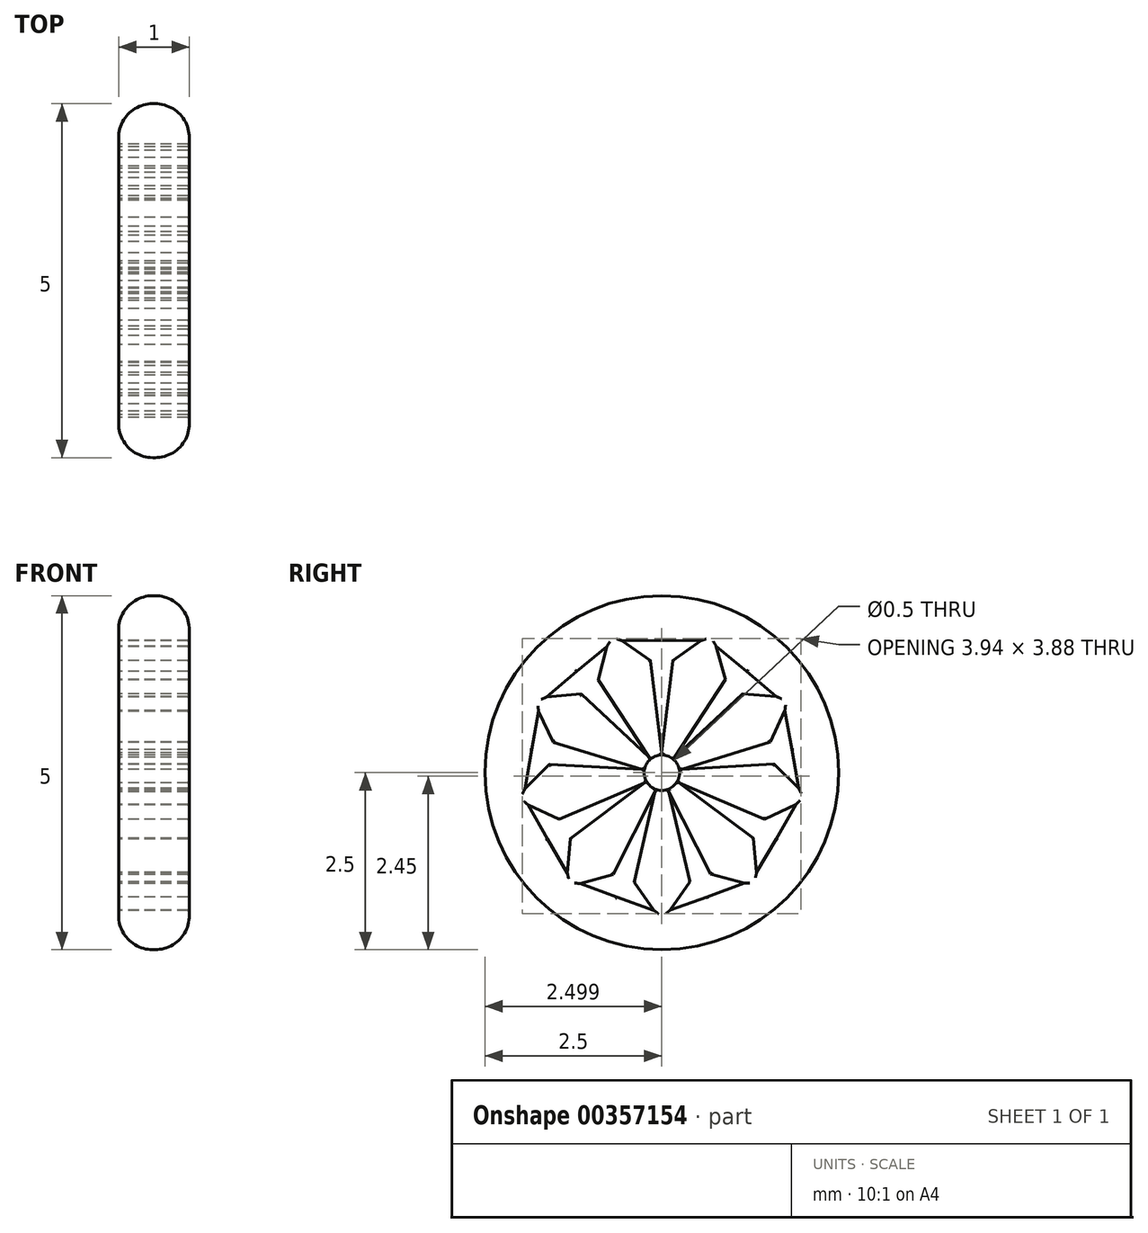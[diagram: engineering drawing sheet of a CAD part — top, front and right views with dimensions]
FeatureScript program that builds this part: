
annotation { "Feature Type Name" : "Feature", "Feature Type Description" : "" }
export const myFeature = defineFeature(function(context is Context, id is Id, definition is map)
    precondition{}
    {
        {
            var Q0;
            Q0=qCreatedBy(makeId("Right.planeOp"),FACE);
            var sketch = newSketch(context, id + "F0", { "sketchPlane" : qUnion([Q0])});
            skCircle(sketch, "E0", {"center": v(0, 0) * mm, "radius": 2.5 * mm});
            skCircle(sketch, "E1", {"center": v(0, 0) * mm, "radius": 2 * mm});
            skCircle(sketch, "E2", {"center": v(0, 0) * mm, "radius": 0.25 * mm});
            skLineSegment(sketch, "E3", {"start": v(0, 1.87) * mm, "end": v(-0.56, 1.86) * mm});
            skLineSegment(sketch, "E4", {"start": v(-0.16, 1.58) * mm, "end": v(-0.56, 1.86) * mm});
            skLineSegment(sketch, "E5", {"start": v(-0.16, 1.58) * mm, "end": v(0, 0.28) * mm});
            skLineSegment(sketch, "E6", {"start": v(0, 0.28) * mm, "end": v(0.16, 1.58) * mm});
            skLineSegment(sketch, "E7", {"start": v(0.16, 1.58) * mm, "end": v(0.55, 1.86) * mm});
            skLineSegment(sketch, "E8", {"start": v(0.55, 1.86) * mm, "end": v(0, 1.87) * mm});
            skLineSegment(sketch, "E9.1.0", {"start": v(-0.9, 1.31) * mm, "end": v(-0.78, 1.78) * mm});
            skLineSegment(sketch, "E9.1.1", {"start": v(-0.78, 1.78) * mm, "end": v(-1.2, 1.43) * mm});
            skLineSegment(sketch, "E9.1.2", {"start": v(-1.2, 1.43) * mm, "end": v(-1.63, 1.07) * mm});
            skLineSegment(sketch, "E9.1.3", {"start": v(-1.14, 1.11) * mm, "end": v(-1.63, 1.07) * mm});
            skLineSegment(sketch, "E9.1.4", {"start": v(-1.14, 1.11) * mm, "end": v(-0.18, 0.22) * mm});
            skLineSegment(sketch, "E9.1.5", {"start": v(-0.18, 0.22) * mm, "end": v(-0.9, 1.31) * mm});
            skLineSegment(sketch, "E9.2.0", {"start": v(-1.53, 0.43) * mm, "end": v(-1.74, 0.86) * mm});
            skLineSegment(sketch, "E9.2.1", {"start": v(-1.74, 0.86) * mm, "end": v(-1.84, 0.32) * mm});
            skLineSegment(sketch, "E9.2.2", {"start": v(-1.84, 0.32) * mm, "end": v(-1.93, -0.23) * mm});
            skLineSegment(sketch, "E9.2.3", {"start": v(-1.59, 0.12) * mm, "end": v(-1.93, -0.23) * mm});
            skLineSegment(sketch, "E9.2.4", {"start": v(-1.59, 0.12) * mm, "end": v(-0.28, 0.05) * mm});
            skLineSegment(sketch, "E9.2.5", {"start": v(-0.28, 0.05) * mm, "end": v(-1.53, 0.43) * mm});
            skLineSegment(sketch, "E9.3.0", {"start": v(-1.45, -0.66) * mm, "end": v(-1.89, -0.46) * mm});
            skLineSegment(sketch, "E9.3.1", {"start": v(-1.89, -0.46) * mm, "end": v(-1.62, -0.93) * mm});
            skLineSegment(sketch, "E9.3.2", {"start": v(-1.62, -0.93) * mm, "end": v(-1.33, -1.42) * mm});
            skLineSegment(sketch, "E9.3.3", {"start": v(-1.3, -0.93) * mm, "end": v(-1.33, -1.42) * mm});
            skLineSegment(sketch, "E9.3.4", {"start": v(-1.3, -0.93) * mm, "end": v(-0.25, -0.14) * mm});
            skLineSegment(sketch, "E9.3.5", {"start": v(-0.25, -0.14) * mm, "end": v(-1.45, -0.66) * mm});
            skLineSegment(sketch, "E9.4.0", {"start": v(-0.69, -1.44) * mm, "end": v(-1.15, -1.56) * mm});
            skLineSegment(sketch, "E9.4.1", {"start": v(-1.15, -1.56) * mm, "end": v(-0.64, -1.76) * mm});
            skLineSegment(sketch, "E9.4.2", {"start": v(-0.64, -1.76) * mm, "end": v(-0.11, -1.94) * mm});
            skLineSegment(sketch, "E9.4.3", {"start": v(-0.4, -1.54) * mm, "end": v(-0.11, -1.94) * mm});
            skLineSegment(sketch, "E9.4.4", {"start": v(-0.4, -1.54) * mm, "end": v(-0.1, -0.27) * mm});
            skLineSegment(sketch, "E9.4.5", {"start": v(-0.1, -0.27) * mm, "end": v(-0.69, -1.44) * mm});
            skLineSegment(sketch, "E9.5.0", {"start": v(0.4, -1.54) * mm, "end": v(0.12, -1.94) * mm});
            skLineSegment(sketch, "E9.5.1", {"start": v(0.12, -1.94) * mm, "end": v(0.64, -1.76) * mm});
            skLineSegment(sketch, "E9.5.2", {"start": v(0.64, -1.76) * mm, "end": v(1.16, -1.56) * mm});
            skLineSegment(sketch, "E9.5.3", {"start": v(0.7, -1.43) * mm, "end": v(1.16, -1.56) * mm});
            skLineSegment(sketch, "E9.5.4", {"start": v(0.7, -1.43) * mm, "end": v(0.1, -0.27) * mm});
            skLineSegment(sketch, "E9.5.5", {"start": v(0.1, -0.27) * mm, "end": v(0.4, -1.54) * mm});
            skLineSegment(sketch, "E9.6.0", {"start": v(1.3, -0.93) * mm, "end": v(1.34, -1.4) * mm});
            skLineSegment(sketch, "E9.6.1", {"start": v(1.34, -1.4) * mm, "end": v(1.62, -0.93) * mm});
            skLineSegment(sketch, "E9.6.2", {"start": v(1.62, -0.93) * mm, "end": v(1.9, -0.45) * mm});
            skLineSegment(sketch, "E9.6.3", {"start": v(1.45, -0.65) * mm, "end": v(1.9, -0.45) * mm});
            skLineSegment(sketch, "E9.6.4", {"start": v(1.45, -0.65) * mm, "end": v(0.25, -0.14) * mm});
            skLineSegment(sketch, "E9.6.5", {"start": v(0.25, -0.14) * mm, "end": v(1.3, -0.93) * mm});
            skLineSegment(sketch, "E9.7.0", {"start": v(1.59, 0.12) * mm, "end": v(1.93, -0.22) * mm});
            skLineSegment(sketch, "E9.7.1", {"start": v(1.93, -0.22) * mm, "end": v(1.84, 0.32) * mm});
            skLineSegment(sketch, "E9.7.2", {"start": v(1.84, 0.32) * mm, "end": v(1.74, 0.88) * mm});
            skLineSegment(sketch, "E9.7.3", {"start": v(1.53, 0.43) * mm, "end": v(1.74, 0.88) * mm});
            skLineSegment(sketch, "E9.7.4", {"start": v(1.53, 0.43) * mm, "end": v(0.28, 0.05) * mm});
            skLineSegment(sketch, "E9.7.5", {"start": v(0.28, 0.05) * mm, "end": v(1.59, 0.12) * mm});
            skLineSegment(sketch, "E9.8.0", {"start": v(1.14, 1.11) * mm, "end": v(1.62, 1.08) * mm});
            skLineSegment(sketch, "E9.8.1", {"start": v(1.62, 1.08) * mm, "end": v(1.2, 1.43) * mm});
            skLineSegment(sketch, "E9.8.2", {"start": v(1.2, 1.43) * mm, "end": v(0.77, 1.79) * mm});
            skLineSegment(sketch, "E9.8.3", {"start": v(0.9, 1.32) * mm, "end": v(0.77, 1.79) * mm});
            skLineSegment(sketch, "E9.8.4", {"start": v(0.9, 1.32) * mm, "end": v(0.18, 0.22) * mm});
            skLineSegment(sketch, "E9.8.5", {"start": v(0.18, 0.22) * mm, "end": v(1.14, 1.11) * mm});
            skSolve(sketch);
        }
        {
            var Q0;
            Q0 = qSketchRegion(id + "F0", true);
            extrude(context, id + "F1", {"entities" : qUnion([Q0]), "depth" : 1 * mm});
        }
        {
            var Q0;
            Q0=makeQuery(id+"F0.imprint","IMPRINT",FACE,{"disambiguationData":[TD([[makeQuery(id+"F0.imprint","IMPRINT",EDGE,{"derivedFrom":sQuery(id+"F0.wireOp",EDGE,"E1")}),1.0]])]});
            extrude(context, id + "F2", {"entities" : qUnion([Q0]), "operationType" : NewBodyOperationType.ADD, "depth" : 1 * mm});
        }
        {
            var Q0;
            Q0=makeQuery(id+"F1.opExtrude","CAP_EDGE",EDGE,{"disambiguationData":[OSD([sQuery(id+"F0.wireOp",EDGE,"E1")])],"isStart":false});
            var Q1;
            Q1=makeQuery(id+"F1.opExtrude","CAP_EDGE",EDGE,{"disambiguationData":[OSD([sQuery(id+"F0.wireOp",EDGE,"E0")])],"isStart":true});
            var Q2;
            Q2=makeQuery(id+"F1.opExtrude","CAP_EDGE",EDGE,{"disambiguationData":[OSD([sQuery(id+"F0.wireOp",EDGE,"E0")])],"isStart":false});
            fillet(context, id + "F3", {"entities" : qUnion([Q0, Q1, Q2]), "radius" : 0.48 * mm, "tangentPropagation" : true, "allowEdgeOverflow" : false});
        }
        {
            var Q0;
            {var subQ0=sQuery(id+"F0.wireOp",EDGE,"E1");Q0=makeQuery(id+"F2.boolean.opBoolean","MERGE",FACE,{"derivedFrom":[makeQuery(id+"F1.opExtrude","CAP_FACE",FACE,{"disambiguationData":[OSD([sQuery(id+"F0.wireOp",EDGE,"E0"),subQ0])],"isStart":false}),makeQuery(id+"F2.opExtrude","CAP_FACE",FACE,{"disambiguationData":[OSD([subQ0,sQuery(id+"F0.wireOp",EDGE,"E2"),sQuery(id+"F0.wireOp",EDGE,"E3"),sQuery(id+"F0.wireOp",EDGE,"E4"),sQuery(id+"F0.wireOp",EDGE,"E5"),sQuery(id+"F0.wireOp",EDGE,"E6"),sQuery(id+"F0.wireOp",EDGE,"E7"),sQuery(id+"F0.wireOp",EDGE,"E8"),sQuery(id+"F0.wireOp",EDGE,"E9.1.0"),sQuery(id+"F0.wireOp",EDGE,"E9.1.1"),sQuery(id+"F0.wireOp",EDGE,"E9.1.2"),sQuery(id+"F0.wireOp",EDGE,"E9.1.3"),sQuery(id+"F0.wireOp",EDGE,"E9.1.4"),sQuery(id+"F0.wireOp",EDGE,"E9.1.5"),sQuery(id+"F0.wireOp",EDGE,"E9.2.0"),sQuery(id+"F0.wireOp",EDGE,"E9.2.1"),sQuery(id+"F0.wireOp",EDGE,"E9.2.2"),sQuery(id+"F0.wireOp",EDGE,"E9.2.3"),sQuery(id+"F0.wireOp",EDGE,"E9.2.4"),sQuery(id+"F0.wireOp",EDGE,"E9.2.5"),sQuery(id+"F0.wireOp",EDGE,"E9.3.0"),sQuery(id+"F0.wireOp",EDGE,"E9.3.1"),sQuery(id+"F0.wireOp",EDGE,"E9.3.2"),sQuery(id+"F0.wireOp",EDGE,"E9.3.3"),sQuery(id+"F0.wireOp",EDGE,"E9.3.4"),sQuery(id+"F0.wireOp",EDGE,"E9.3.5"),sQuery(id+"F0.wireOp",EDGE,"E9.4.0"),sQuery(id+"F0.wireOp",EDGE,"E9.4.1"),sQuery(id+"F0.wireOp",EDGE,"E9.4.2"),sQuery(id+"F0.wireOp",EDGE,"E9.4.3"),sQuery(id+"F0.wireOp",EDGE,"E9.4.4"),sQuery(id+"F0.wireOp",EDGE,"E9.4.5"),sQuery(id+"F0.wireOp",EDGE,"E9.5.0"),sQuery(id+"F0.wireOp",EDGE,"E9.5.1"),sQuery(id+"F0.wireOp",EDGE,"E9.5.2"),sQuery(id+"F0.wireOp",EDGE,"E9.5.3"),sQuery(id+"F0.wireOp",EDGE,"E9.5.4"),sQuery(id+"F0.wireOp",EDGE,"E9.5.5"),sQuery(id+"F0.wireOp",EDGE,"E9.6.0"),sQuery(id+"F0.wireOp",EDGE,"E9.6.1"),sQuery(id+"F0.wireOp",EDGE,"E9.6.2"),sQuery(id+"F0.wireOp",EDGE,"E9.6.3"),sQuery(id+"F0.wireOp",EDGE,"E9.6.4"),sQuery(id+"F0.wireOp",EDGE,"E9.6.5"),sQuery(id+"F0.wireOp",EDGE,"E9.7.0"),sQuery(id+"F0.wireOp",EDGE,"E9.7.1"),sQuery(id+"F0.wireOp",EDGE,"E9.7.2"),sQuery(id+"F0.wireOp",EDGE,"E9.7.3"),sQuery(id+"F0.wireOp",EDGE,"E9.7.4"),sQuery(id+"F0.wireOp",EDGE,"E9.7.5"),sQuery(id+"F0.wireOp",EDGE,"E9.8.0"),sQuery(id+"F0.wireOp",EDGE,"E9.8.1"),sQuery(id+"F0.wireOp",EDGE,"E9.8.2"),sQuery(id+"F0.wireOp",EDGE,"E9.8.3"),sQuery(id+"F0.wireOp",EDGE,"E9.8.4"),sQuery(id+"F0.wireOp",EDGE,"E9.8.5")])],"isStart":false})]});}
            var Q1;
            {var subQ0=sQuery(id+"F0.wireOp",EDGE,"E1");Q1=makeQuery(id+"F2.boolean.opBoolean","MERGE",FACE,{"derivedFrom":[makeQuery(id+"F1.opExtrude","CAP_FACE",FACE,{"disambiguationData":[OSD([sQuery(id+"F0.wireOp",EDGE,"E0"),subQ0])],"isStart":true}),makeQuery(id+"F2.opExtrude","CAP_FACE",FACE,{"disambiguationData":[OSD([subQ0,sQuery(id+"F0.wireOp",EDGE,"E2"),sQuery(id+"F0.wireOp",EDGE,"E3"),sQuery(id+"F0.wireOp",EDGE,"E4"),sQuery(id+"F0.wireOp",EDGE,"E5"),sQuery(id+"F0.wireOp",EDGE,"E6"),sQuery(id+"F0.wireOp",EDGE,"E7"),sQuery(id+"F0.wireOp",EDGE,"E8"),sQuery(id+"F0.wireOp",EDGE,"E9.1.0"),sQuery(id+"F0.wireOp",EDGE,"E9.1.1"),sQuery(id+"F0.wireOp",EDGE,"E9.1.2"),sQuery(id+"F0.wireOp",EDGE,"E9.1.3"),sQuery(id+"F0.wireOp",EDGE,"E9.1.4"),sQuery(id+"F0.wireOp",EDGE,"E9.1.5"),sQuery(id+"F0.wireOp",EDGE,"E9.2.0"),sQuery(id+"F0.wireOp",EDGE,"E9.2.1"),sQuery(id+"F0.wireOp",EDGE,"E9.2.2"),sQuery(id+"F0.wireOp",EDGE,"E9.2.3"),sQuery(id+"F0.wireOp",EDGE,"E9.2.4"),sQuery(id+"F0.wireOp",EDGE,"E9.2.5"),sQuery(id+"F0.wireOp",EDGE,"E9.3.0"),sQuery(id+"F0.wireOp",EDGE,"E9.3.1"),sQuery(id+"F0.wireOp",EDGE,"E9.3.2"),sQuery(id+"F0.wireOp",EDGE,"E9.3.3"),sQuery(id+"F0.wireOp",EDGE,"E9.3.4"),sQuery(id+"F0.wireOp",EDGE,"E9.3.5"),sQuery(id+"F0.wireOp",EDGE,"E9.4.0"),sQuery(id+"F0.wireOp",EDGE,"E9.4.1"),sQuery(id+"F0.wireOp",EDGE,"E9.4.2"),sQuery(id+"F0.wireOp",EDGE,"E9.4.3"),sQuery(id+"F0.wireOp",EDGE,"E9.4.4"),sQuery(id+"F0.wireOp",EDGE,"E9.4.5"),sQuery(id+"F0.wireOp",EDGE,"E9.5.0"),sQuery(id+"F0.wireOp",EDGE,"E9.5.1"),sQuery(id+"F0.wireOp",EDGE,"E9.5.2"),sQuery(id+"F0.wireOp",EDGE,"E9.5.3"),sQuery(id+"F0.wireOp",EDGE,"E9.5.4"),sQuery(id+"F0.wireOp",EDGE,"E9.5.5"),sQuery(id+"F0.wireOp",EDGE,"E9.6.0"),sQuery(id+"F0.wireOp",EDGE,"E9.6.1"),sQuery(id+"F0.wireOp",EDGE,"E9.6.2"),sQuery(id+"F0.wireOp",EDGE,"E9.6.3"),sQuery(id+"F0.wireOp",EDGE,"E9.6.4"),sQuery(id+"F0.wireOp",EDGE,"E9.6.5"),sQuery(id+"F0.wireOp",EDGE,"E9.7.0"),sQuery(id+"F0.wireOp",EDGE,"E9.7.1"),sQuery(id+"F0.wireOp",EDGE,"E9.7.2"),sQuery(id+"F0.wireOp",EDGE,"E9.7.3"),sQuery(id+"F0.wireOp",EDGE,"E9.7.4"),sQuery(id+"F0.wireOp",EDGE,"E9.7.5"),sQuery(id+"F0.wireOp",EDGE,"E9.8.0"),sQuery(id+"F0.wireOp",EDGE,"E9.8.1"),sQuery(id+"F0.wireOp",EDGE,"E9.8.2"),sQuery(id+"F0.wireOp",EDGE,"E9.8.3"),sQuery(id+"F0.wireOp",EDGE,"E9.8.4"),sQuery(id+"F0.wireOp",EDGE,"E9.8.5")])],"isStart":true})]});}
            fillet(context, id + "F4", {"entities" : qUnion([Q0, Q1]), "radius" : 0.02 * mm, "tangentPropagation" : true, "allowEdgeOverflow" : false});
        }
    });
